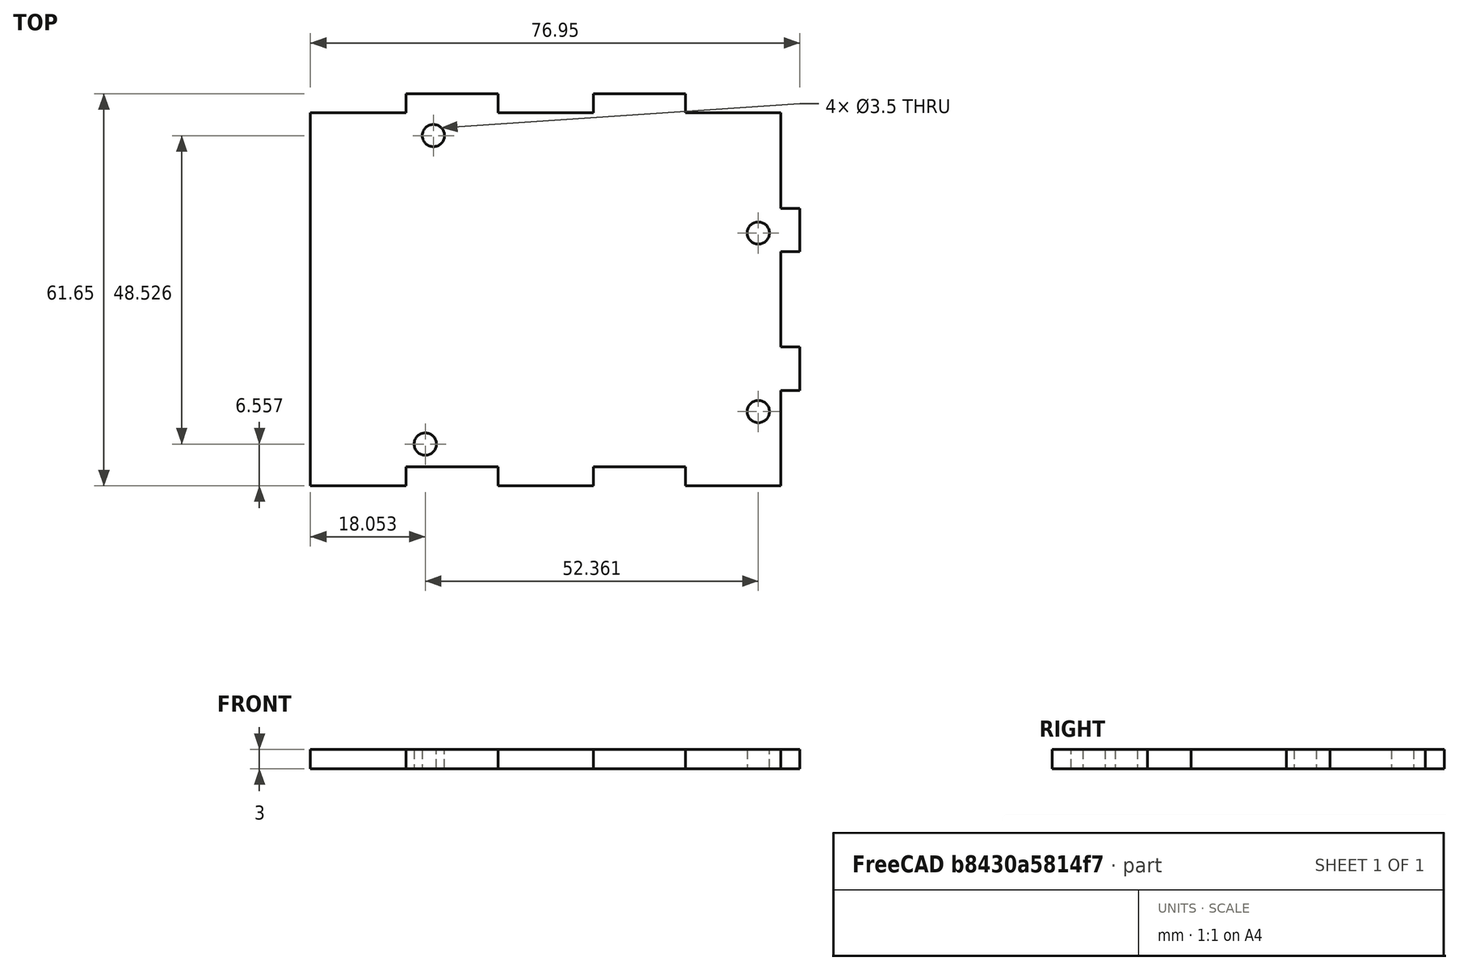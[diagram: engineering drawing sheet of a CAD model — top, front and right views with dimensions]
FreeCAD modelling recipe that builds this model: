
FCSTD DOCUMENT  (FreeCAD 0.19R)
Label: CAIXA-ARDUINO_03
License: Creative Commons Attribution-NonCommercial
LicenseURL: http://creativecommons.org/licenses/by-nc/4.0/
objects: Spreadsheet::Sheet×1, Part::Feature×1, Sketcher::SketchObject×1, Part::Extrusion×1
note: 3 computed .brp shape members not serialized (recipe doc carries the construction recipe); baked Part::Feature solids carry a one-line shape summary decoded from their .brp

FEATURE [Spreadsheet::Sheet] Spreadsheet
  cells = A1=Espessura; B1(wall)=3; A2=Altura; B2(height)=15; A3=Furo; B3(diameter)=3.5; A4=Conector A; B4(conectorA)=15; A5=Conector B; B5(conectorB)=10; A6=Conector C; B6(conectorC)=5; A7=Folga; B7(space)=1
FEATURE [Part::Feature] ARDUINO_3D_SCALED
  Placement = pos=(0,0,4) rot=(0,0,1;0rad)
  shape: bbox 75.35 x 53.65 x 13.2 mm, 104 faces, 0 solids (baked)
  expr: .Placement.Base.z = Spreadsheet.wall + Spreadsheet.space
FEATURE [Sketcher::SketchObject] Sketch  label="Base001"
  ExternalGeometry = -> [ARDUINO_3D_SCALED]
  expr: Constraints[31] = Spreadsheet.wall
  expr: Constraints[139] = Spreadsheet.conectorA
  expr: Constraints[7] = Spreadsheet.diameter
  expr: Constraints[19] = Spreadsheet.space
  sketch-geometry (60):
    g0: Circle CenterX=14.0525 CenterY=2.55698 CenterZ=0 NormalX=0 NormalY=0 NormalZ=1 AngleXU=0 Radius=1.75
    g1: Circle CenterX=66.4139 CenterY=7.6684 CenterZ=0 NormalX=0 NormalY=0 NormalZ=1 AngleXU=0 Radius=1.75
    g2: Circle CenterX=66.41 CenterY=35.7498 CenterZ=0 NormalX=0 NormalY=0 NormalZ=1 AngleXU=0 Radius=1.75
    g3: Circle CenterX=15.3341 CenterY=51.0829 CenterZ=0 NormalX=0 NormalY=0 NormalZ=1 AngleXU=0 Radius=1.75
    g4: LineSegment [constr] StartX=32.925 StartY=53.65 StartZ=0 EndX=32.925 EndY=54.65 EndZ=0
    g5: LineSegment [constr] StartX=-1e-16 StartY=22.75 StartZ=0 EndX=-1 EndY=22.75 EndZ=0
    g6: LineSegment [constr] StartX=68.95 StartY=21.575 StartZ=0 EndX=69.95 EndY=21.575 EndZ=0
    g7: LineSegment [constr] StartX=33.2 StartY=4e-16 StartZ=0 EndX=33.2 EndY=-1 EndZ=0
    g8: LineSegment StartX=32.925 StartY=54.65 StartZ=0 EndX=32.925 EndY=57.65 EndZ=0
    g9: LineSegment [constr] StartX=69.95 StartY=21.575 StartZ=0 EndX=72.95 EndY=21.575 EndZ=0
    g10: LineSegment [constr] StartX=33.2 StartY=-1 StartZ=0 EndX=33.2 EndY=-4 EndZ=0
    g11: LineSegment [constr] StartX=-1 StartY=22.75 StartZ=0 EndX=-4 EndY=22.75 EndZ=0
    g12: LineSegment [constr] StartX=-4 StartY=54.65 StartZ=0 EndX=11 EndY=54.65 EndZ=0
    g13: LineSegment [constr] StartX=11 StartY=54.65 StartZ=0 EndX=11 EndY=57.65 EndZ=0
    g14: LineSegment [constr] StartX=11 StartY=57.65 StartZ=0 EndX=25.475 EndY=57.65 EndZ=0
    g15: LineSegment [constr] StartX=25.475 StartY=57.65 StartZ=0 EndX=25.475 EndY=54.65 EndZ=0
    g16: LineSegment [constr] StartX=25.475 StartY=54.65 StartZ=0 EndX=40.475 EndY=54.65 EndZ=0
    g17: LineSegment [constr] StartX=40.475 StartY=54.65 StartZ=0 EndX=40.475 EndY=57.65 EndZ=0
    g18: LineSegment [constr] StartX=40.475 StartY=57.65 StartZ=0 EndX=54.95 EndY=57.65 EndZ=0
    g19: LineSegment [constr] StartX=54.95 StartY=57.65 StartZ=0 EndX=54.95 EndY=54.65 EndZ=0
    g20: LineSegment [constr] StartX=54.95 StartY=54.65 StartZ=0 EndX=69.95 EndY=54.65 EndZ=0
    g21: LineSegment StartX=69.95 StartY=40.6581 StartZ=0 EndX=72.95 EndY=40.6581 EndZ=0
    g22: LineSegment StartX=72.95 StartY=40.6581 StartZ=0 EndX=72.95 EndY=33.4299 EndZ=0
    g23: LineSegment StartX=72.95 StartY=33.4299 StartZ=0 EndX=69.95 EndY=33.4299 EndZ=0
    g24: LineSegment StartX=69.95 StartY=33.4299 StartZ=0 EndX=69.95 EndY=18.0266 EndZ=0
    g25: LineSegment StartX=69.95 StartY=18.0266 StartZ=0 EndX=72.95 EndY=18.0266 EndZ=0
    g26: LineSegment StartX=72.95 StartY=18.0266 StartZ=0 EndX=72.95 EndY=10.7984 EndZ=0
    g27: LineSegment StartX=72.95 StartY=10.7984 StartZ=0 EndX=69.95 EndY=10.7984 EndZ=0
    g28: LineSegment StartX=69.95 StartY=10.7984 StartZ=0 EndX=69.95 EndY=-4 EndZ=0
    g29: LineSegment StartX=69.95 StartY=-4 StartZ=0 EndX=54.95 EndY=-4 EndZ=0
    g30: LineSegment StartX=54.95 StartY=-4 StartZ=0 EndX=54.95 EndY=-1 EndZ=0
    g31: LineSegment StartX=54.95 StartY=-1 StartZ=0 EndX=40.475 EndY=-1 EndZ=0
    g32: LineSegment StartX=40.475 StartY=-1 StartZ=0 EndX=40.475 EndY=-4 EndZ=0
    g33: LineSegment StartX=40.475 StartY=-4 StartZ=0 EndX=25.475 EndY=-4 EndZ=0
    g34: LineSegment StartX=25.475 StartY=-4 StartZ=0 EndX=25.475 EndY=-1 EndZ=0
    g35: LineSegment StartX=25.475 StartY=-1 StartZ=0 EndX=11 EndY=-1 EndZ=0
    g36: LineSegment StartX=11 StartY=-1 StartZ=0 EndX=11 EndY=-4 EndZ=0
    g37: LineSegment StartX=11 StartY=-4 StartZ=0 EndX=-4 EndY=-4 EndZ=0
    g38: LineSegment StartX=-4 StartY=-4 StartZ=0 EndX=-4 EndY=54.65 EndZ=0
    g39: LineSegment StartX=11 StartY=57.65 StartZ=0 EndX=-4 EndY=57.65 EndZ=0
    g40: LineSegment StartX=-4 StartY=57.65 StartZ=0 EndX=-4 EndY=54.65 EndZ=0
    g41: LineSegment StartX=11 StartY=54.65 StartZ=0 EndX=25.475 EndY=54.65 EndZ=0
    g42: LineSegment StartX=25.475 StartY=57.65 StartZ=0 EndX=40.475 EndY=57.65 EndZ=0
    g43: LineSegment StartX=40.475 StartY=54.65 StartZ=0 EndX=54.95 EndY=54.65 EndZ=0
    g44: LineSegment [constr] StartX=72.95 StartY=57.65 StartZ=0 EndX=69.95 EndY=57.65 EndZ=0
    g45: LineSegment StartX=54.95 StartY=57.65 StartZ=0 EndX=69.95 EndY=57.65 EndZ=0
    g46: LineSegment [constr] StartX=69.95 StartY=40.6581 StartZ=0 EndX=69.95 EndY=33.4299 EndZ=0
    g47: LineSegment [constr] StartX=72.95 StartY=33.4299 StartZ=0 EndX=72.95 EndY=18.0266 EndZ=0
    g48: LineSegment [constr] StartX=69.95 StartY=-1 StartZ=0 EndX=69.95 EndY=-4 EndZ=0
    g49: LineSegment [constr] StartX=69.95 StartY=-1 StartZ=0 EndX=54.95 EndY=-1 EndZ=0
    g50: LineSegment [constr] StartX=54.95 StartY=-4 StartZ=0 EndX=40.475 EndY=-4 EndZ=0
    g51: LineSegment [constr] StartX=40.475 StartY=-1 StartZ=0 EndX=25.475 EndY=-1 EndZ=0
    g52: LineSegment [constr] StartX=25.475 StartY=-4 StartZ=0 EndX=11 EndY=-4 EndZ=0
    g53: LineSegment [constr] StartX=-4 StartY=-4 StartZ=0 EndX=-4 EndY=-1 EndZ=0
    g54: LineSegment [constr] StartX=-4 StartY=-1 StartZ=0 EndX=11 EndY=-1 EndZ=0
    g55: LineSegment [constr] StartX=69.95 StartY=18.0266 StartZ=0 EndX=69.95 EndY=10.7984 EndZ=0
    g56: LineSegment StartX=69.95 StartY=57.65 StartZ=0 EndX=69.95 EndY=40.6581 EndZ=0
    g57: LineSegment [constr] StartX=72.95 StartY=10.7984 StartZ=0 EndX=72.95 EndY=-4 EndZ=0
    g58: LineSegment [constr] StartX=72.95 StartY=-4 StartZ=0 EndX=69.95 EndY=-4 EndZ=0
    g59: LineSegment [constr] StartX=72.95 StartY=57.65 StartZ=0 EndX=72.95 EndY=40.6581 EndZ=0
  constraints (156):
    c: Coincident(g0,g-22)
    c: Coincident(g1,g-23)
    c: Coincident(g2,g-20)
    c: Coincident(g3,g-21)
    c: Equal(g3,g2)
    c: Equal(g2,g1)
    c: Equal(g1,g0)
    c: Diameter(g3) = 3.5
    c: Vertical(g4)
    c: Horizontal(g5)
    c: Horizontal(g6)
    c: Vertical(g7)
    c: Equal(g5,g4)
    c: Equal(g4,g6)
    c: Equal(g6,g7)
    c: Symmetric(g-12,g-12,g7)
    c: Symmetric(g-16,g-16,g6)
    c: Symmetric(g-3,g-3,g4)
    c: Symmetric(g-8,g-8,g5)
    c: DistanceY(g4,g4) = 1
    c: Coincident(g8,g4)
    c: Vertical(g8)
    c: Coincident(g9,g6)
    c: Horizontal(g9)
    c: Coincident(g10,g7)
    c: Vertical(g10)
    c: Coincident(g11,g5)
    c: Horizontal(g11)
    c: Equal(g11,g10)
    c: Equal(g10,g9)
    c: Equal(g9,g8)
    c: DistanceY(g8,g8) = 3
    c: Horizontal(g12)
    c: Coincident(g12,g13)
    c: Vertical(g13)
    c: Coincident(g13,g14)
    c: Horizontal(g14)
    c: Coincident(g14,g15)
    c: Vertical(g15)
    c: Coincident(g15,g16)
    c: Horizontal(g16)
    c: Coincident(g16,g17)
    c: Vertical(g17)
    c: Coincident(g17,g18)
    c: Horizontal(g18)
    c: Coincident(g18,g19)
    c: Coincident(g19,g20)
    c: Horizontal(g20)
    c: Horizontal(g21)
    c: Coincident(g21,g22)
    c: Vertical(g22)
    c: Coincident(g22,g23)
    c: Horizontal(g23)
    c: Coincident(g23,g24)
    c: Vertical(g24)
    c: Coincident(g24,g25)
    c: Horizontal(g25)
    c: Coincident(g25,g26)
    c: Vertical(g26)
    c: Coincident(g26,g27)
    c: Horizontal(g27)
    c: Coincident(g27,g28)
    c: Vertical(g28)
    c: Coincident(g28,g29)
    c: Horizontal(g29)
    c: Coincident(g29,g30)
    c: Coincident(g30,g31)
    c: Horizontal(g31)
    c: Coincident(g31,g32)
    c: Coincident(g32,g33)
    c: Horizontal(g33)
    c: Coincident(g33,g34)
    c: Vertical(g34)
    c: Coincident(g34,g35)
    c: Horizontal(g35)
    c: Coincident(g35,g36)
    c: Coincident(g36,g37)
    c: Horizontal(g37)
    c: Coincident(g37,g38)
    c: Coincident(g38,g12)
    c: Vertical(g38)
    c: Coincident(g13,g39)
    c: Horizontal(g39)
    c: Coincident(g39,g40)
    c: Coincident(g40,g12)
    c: Vertical(g40)
    c: Coincident(g12,g41)
    c: Coincident(g41,g15)
    c: Horizontal(g41)
    c: Coincident(g14,g42)
    c: Coincident(g42,g17)
    c: Horizontal(g42)
    c: Coincident(g16,g43)
    c: Coincident(g43,g19)
    c: Horizontal(g43)
    c: Vertical(g19)
    c: Horizontal(g44)
    c: Coincident(g45,g18)
    c: Coincident(g45,g44)
    c: Horizontal(g45)
    c: Coincident(g46,g23)
    c: Vertical(g46)
    c: Coincident(g47,g22)
    c: Coincident(g47,g25)
    c: Vertical(g47)
    c: Vertical(g48)
    c: Coincident(g49,g30)
    c: Horizontal(g49)
    c: Vertical(g30)
    c: Vertical(g32)
    c: Coincident(g50,g29)
    c: Coincident(g50,g32)
    c: Horizontal(g50)
    c: Vertical(g36)
    c: Coincident(g51,g31)
    c: Coincident(g51,g34)
    c: Horizontal(g51)
    c: Coincident(g52,g33)
    c: Horizontal(g52)
    c: Coincident(g36,g52)
    c: Coincident(g37,g53)
    c: Vertical(g53)
    c: Coincident(g53,g54)
    c: Coincident(g54,g35)
    c: Horizontal(g54)
    c: PointOnObject(g8,g42)
    c: PointOnObject(g9,g47)
    c: PointOnObject(g4,g16)
    c: PointOnObject(g11,g38)
    c: Equal(g54,g51)
    c: Equal(g51,g49)
    c: Equal(g45,g42)
    c: Equal(g42,g39)
    c: Coincident(g55,g27)
    c: Vertical(g55)
    c: Coincident(g24,g55)
    c: Equal(g26,g22)
    c: Equal(g52,g50)
    c: Equal(g14,g18)
    c: DistanceX(g39,g39) = 15
    c: PointOnObject(g6,g24)
    c: PointOnObject(g7,g51)
    c: PointOnObject(g10,g33)
    c: Coincident(g56,g45)
    c: Coincident(g56,g21)
    c: Vertical(g56)
    c: PointOnObject(g20,g56)
    c: Coincident(g21,g46)
    c: Coincident(g26,g57)
    c: Vertical(g57)
    c: Coincident(g57,g58)
    c: Coincident(g58,g28)
    c: Horizontal(g58)
    c: Coincident(g44,g59)
    c: Coincident(g59,g21)
    c: Vertical(g59)
FEATURE [Part::Extrusion] Extrude  label="Base"
  Base = -> Sketch
  Dir = (0,0,1)
  DirMode = 2
  FaceMakerClass = Part::FaceMakerBullseye
  LengthFwd = 3
  LengthRev = 0
  Solid = true
  Symmetric = false
  expr: LengthFwd = Spreadsheet.wall
